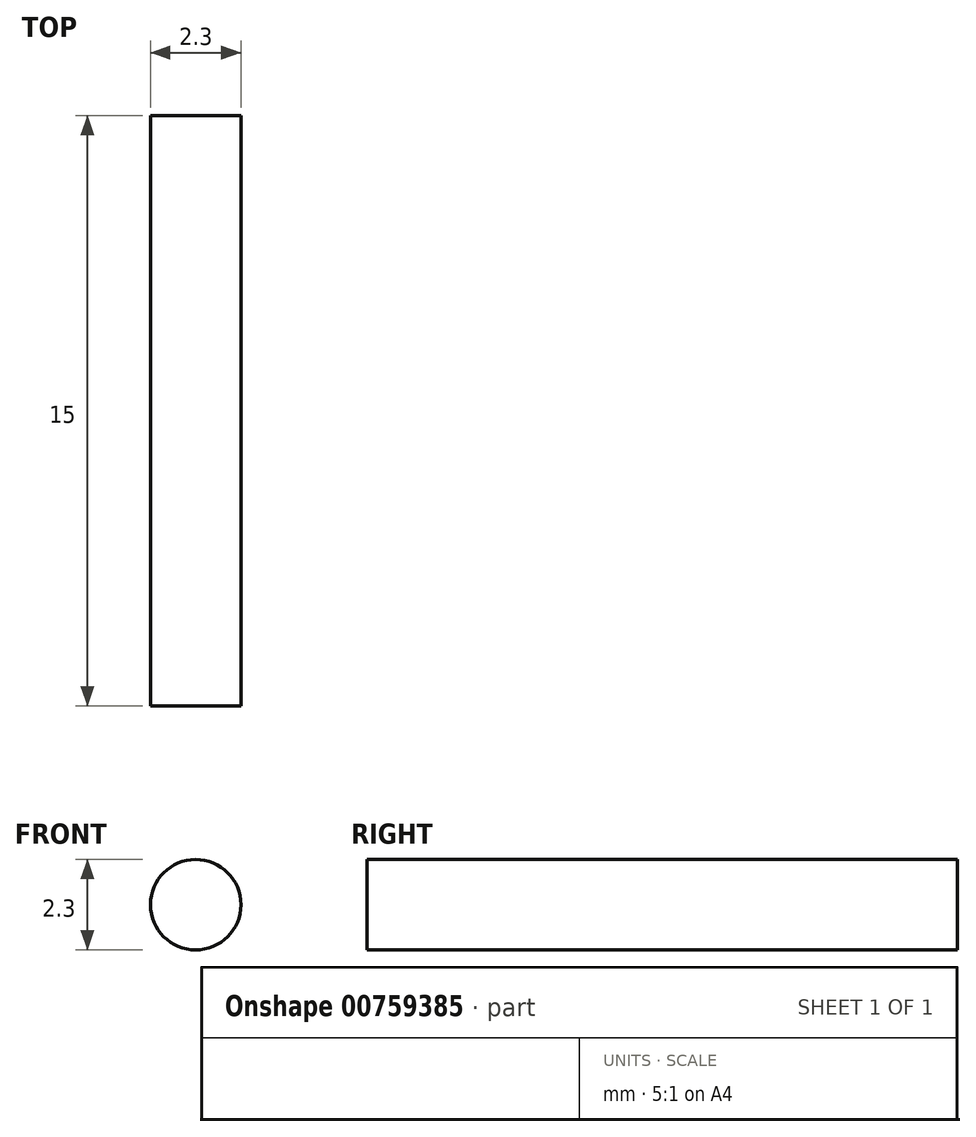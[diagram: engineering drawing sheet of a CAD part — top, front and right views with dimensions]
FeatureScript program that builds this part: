
annotation { "Feature Type Name" : "Feature", "Feature Type Description" : "" }
export const myFeature = defineFeature(function(context is Context, id is Id, definition is map)
    precondition{}
    {
        {
            var Q0;
            Q0=qCreatedBy(makeId("Front.planeOp"),FACE);
            var sketch = newSketch(context, id + "F0", { "sketchPlane" : qUnion([Q0])});
            skCircle(sketch, "E0", {"center": v(0, 0) * mm, "radius": 1.15 * mm});
            skSolve(sketch);
        }
        {
            var Q0;
            Q0 = qSketchRegion(id + "F0", true);
            var Q1;
            Q1=makeQuery(id+"F0.imprint","IMPRINT",FACE,{"disambiguationData":[TD([[makeQuery(id+"F0.imprint","IMPRINT",EDGE,{"derivedFrom":sQuery(id+"F0.wireOp",EDGE,"E0")}),1.0]])]});
            extrude(context, id + "F1", {"entities" : qUnion([Q0, Q1]), "oppositeDirection" : true, "depth" : 15 * mm, "offsetDistance" : 25 * mm});
        }
    });
